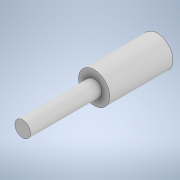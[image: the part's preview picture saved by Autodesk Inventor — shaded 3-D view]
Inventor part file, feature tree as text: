
AUTODESK INVENTOR PART (.ipt)
format: ipt  version: 2022 (Build 260153000, 153)  size: 110,080 bytes
history: native  units: in
note: dims shown in document units (in); Inventor stores cm internally (conversion verified against a paired STEP export)
features: extrude x3, sketch x3, other x2, reference x1
ambient origin geometry x8: Origin, YZ Plane, XZ Plane, XY Plane, X Axis, Y Axis, Z Axis, Center Point
bodies: Solid1 (feature_tree)
feature tree (9):
  extrude  "Extrusion1"  Depth=0.9562in TaperAngle=0.0deg
  extrude  "Extrusion2"  Depth=1.0812in TaperAngle=0.0deg
  extrude  "Extrusion3"  [1 undecoded]
  sketch  "Sketch1"  dims[d0=0.4724in d1=0.9562in d2=0.0in]
  reference  "Reference1"
  sketch  "Sketch2"  dims[d3=0.2362in d4=1.0812in d5=0.0in]
  sketch  "Sketch3"  dims[d6=0.3937in d7=0.0in]
  parser-record x1  (decoder bookkeeping rows leaked as tree rows — omitted from the tree; the rows remain in map.json)
  other  "model.iam"
note: 1 required parameter value undecoded (feature->parameter linkage not recoverable at this tier; creation-order binding heuristic only, values carry confidence <= 0.55)
note: 1 file-system path scrubbed to <path> (originals preserved in map.json)
